# Revit family: Absperrventil 4218 AGF
name_source: partatom
category: Rohrzubehör
revit_build: Autodesk Revit 2018 (Build: 20190510_1515(x64)
units: mm (PartAtom-declared; Revit-internal decimal feet)

## family parameters
Arbeitsebenenbasiert = Nein
Beim Laden mit Abzugskörper schneiden = Nein
Bemaßung runder Anschluss = Durchmesser verwenden
Gemeinsam genutzt = Nein
Immer vertikal = Ja
Teiletyp = Unterbricht

## types (1)
- Absperrventil 4218 AGF
    Anwendungsgebiet = Zum Absperren von Verteilleitungen in Heiz- oder Kühlanlagen, Strängen, Wärmetauschern, Heiz- und
Kühlregistern.
    Hersteller = HERZ-Armaturen Ges.m.b.H
    Hinweise zum Material = Gemäß Art 33 der REACH-Verordnung (EG Nr. 1907/2006) sind wir verpflichtet, darauf hinzuweisen, dass der
Stoff Blei auf der SVHC-Liste geführt wird und dass alle aus Messing bestehenden Bauteile, die in unseren
Erzeugnissen verarbeitet sind, mehr als 0,1 % (w/w) Blei (CAS: 7439-92-1 / EINECS: 231-100-4) enthalten. Da Blei
als Legierungsbestandteil fest gebunden ist, sind keine Expositionen zu erwarten und daher sind keine zusätzlichen
Angaben zur sicheren Verwendung notwendig.

Grundanstrich basierent auf Alkydharze (Kunstharzgrundierung) und enthält blei- und chromatfreie Rost- schutzpigmente. Deckbeschichtung mit Epoxidharz. Lösungsmittelgehalt ist geringer als in der VOCAnlagen-Verordnung 2002 zulässig.
Glanzgrad: matt
Schichtstärke trocken (TSD) : ~ 100 μm
    Max. Betriebsdruck = 1600000.0 Pa
    Max. Betriebstemperatur ab DN 40 = 110 °C
    Max. Betriebstemperatur bis DN 32 = 130 °C
    Medium = Heizwasserqualität entsprechend ÖNORM H 5195 bzw. VDI Richtlinie 2035. Ethylen und Propylenglykol
können in einem Verhältnis von 25-50 vol. [%] gemischt werden.
    O-Ringe = EPDM
    PN = 16
    SCRNCODE = 05;11;2
    SCRNSEQ = ARM;ARM_TYP="ABSV";2
    URL = www.herz-armaturen.at
    Ventilgehäuse = Grauguss GJL 250 nach EN 1561
    Ventiloberteil = Messing
    w = 10.00°
